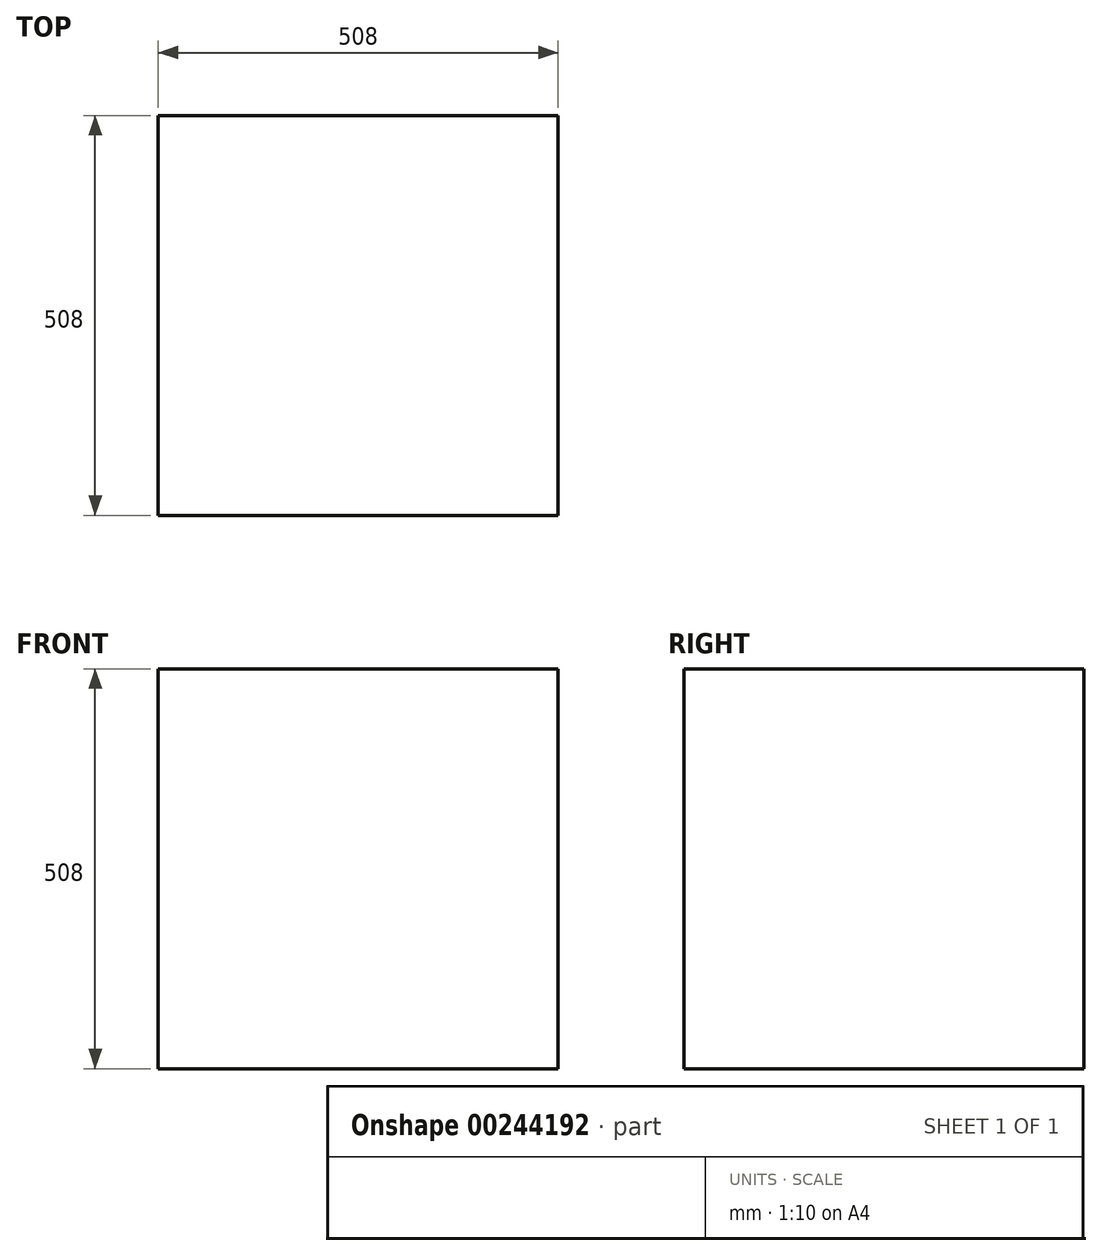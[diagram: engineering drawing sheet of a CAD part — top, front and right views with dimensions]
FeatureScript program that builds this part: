
annotation { "Feature Type Name" : "Feature", "Feature Type Description" : "" }
export const myFeature = defineFeature(function(context is Context, id is Id, definition is map)
    precondition{}
    {
        {
            var Q0;
            Q0=qCreatedBy(makeId("Top.planeOp"),FACE);
            var sketch = newSketch(context, id + "F0", { "sketchPlane" : qUnion([Q0])});
            skLineSegment(sketch, "E0.bottom", {"start": v(213.15, 228.42) * mm, "end": v(-294.85, 228.42) * mm});
            skLineSegment(sketch, "E0.top", {"start": v(213.15, -279.58) * mm, "end": v(-294.85, -279.58) * mm});
            skLineSegment(sketch, "E0.left", {"start": v(213.15, 228.42) * mm, "end": v(213.15, -279.58) * mm});
            skLineSegment(sketch, "E0.right", {"start": v(-294.85, 228.42) * mm, "end": v(-294.85, -279.58) * mm});
            skSolve(sketch);
        }
        {
            var Q0;
            Q0=makeQuery(id+"F0.imprint","IMPRINT",FACE,{"disambiguationData":[TD([[makeQuery(id+"F0.imprint","IMPRINT",EDGE,{"derivedFrom":sQuery(id+"F0.wireOp",EDGE,"E0.bottom")}),1.0]])]});
            extrude(context, id + "F1", {"entities" : qUnion([Q0]), "depth" : 508 * mm});
        }
    });
